# Revit family: 3DCAD_LGH-160_200RVX3-E
name_source: partatom
category: 機械設備
revit_build: Autodesk Revit 2018 (Build: 20180423_1000(x64)
units: mm (PartAtom-declared; Revit-internal decimal feet)

## family parameters
OmniClass タイトル = Climate Control (HVAC)
OmniClass 番号 = 23.75.00.00
パーツ タイプ = 標準
ロード時にボイドで切り取り = いいえ
丸型コネクタ寸法 = 直径を使用
作業面ベース = いいえ
共有 = いいえ
常に垂直 = はい
部屋計算ポイント = いいえ

## types (4) — shared parameters
Air pipe_Length = 79
Air pipe_diameter 1 = 242  [stored 0.793963 ft]
Air pipe_diameter 2 = 258  [stored 0.846457 ft]
Box_H = 105
Box_W = 119
Center Height = 404  [stored 1.32546 ft]
D = 1144
Distance of Center Height and Air pipes = 40  [stored 0.131234 ft]
H = 808  [stored 2.65092 ft]
Mounting pitch 2 = 1010  [stored 3.31365 ft]
Space View = はい
URL = http://global.mitsubishielectric.com
Upper Unit-LEG Distance = 404  [stored 1.32546 ft]
製造元 = Mitsubishi Electric Corporation
説明 = LOSSNAY

## per-type parameters (varying)
| type | Distance of Air pipes | Electrical power supply | Hertz | Mounting pitch 1 | W | Weight | モデル |
| LGH-160RVX3-E_50Hz | 690  [stored 2.26378 ft] | 220-240 V | 50.0 Hz | 1045  [stored 3.42848 ft] | 1004  [stored 3.29396 ft] | 96.00 kg | LGH-160RVX3-E |
| LGH-200RVX3-E_50Hz | 917  [stored 3.00853 ft] | 220-240 V | 50.0 Hz | 1272  [stored 4.17323 ft] | 1231  [stored 4.03871 ft] | 108.00 kg | LGH-200RVX3-E |
| LGH-160RVX3-E_60Hz | 690  [stored 2.26378 ft] | 220 V | 60.0 Hz | 1045  [stored 3.42848 ft] | 1004  [stored 3.29396 ft] | 96.00 kg | LGH-160RVX3-E |
| LGH-200RVX3-E_60Hz | 917  [stored 3.00853 ft] | 220 V | 60.0 Hz | 1272  [stored 4.17323 ft] | 1231  [stored 4.03871 ft] | 108.00 kg | LGH-200RVX3-E |

note: [stored X ft] marks values corroborated as IEEE doubles in the binary element streams (Revit-internal decimal feet)
